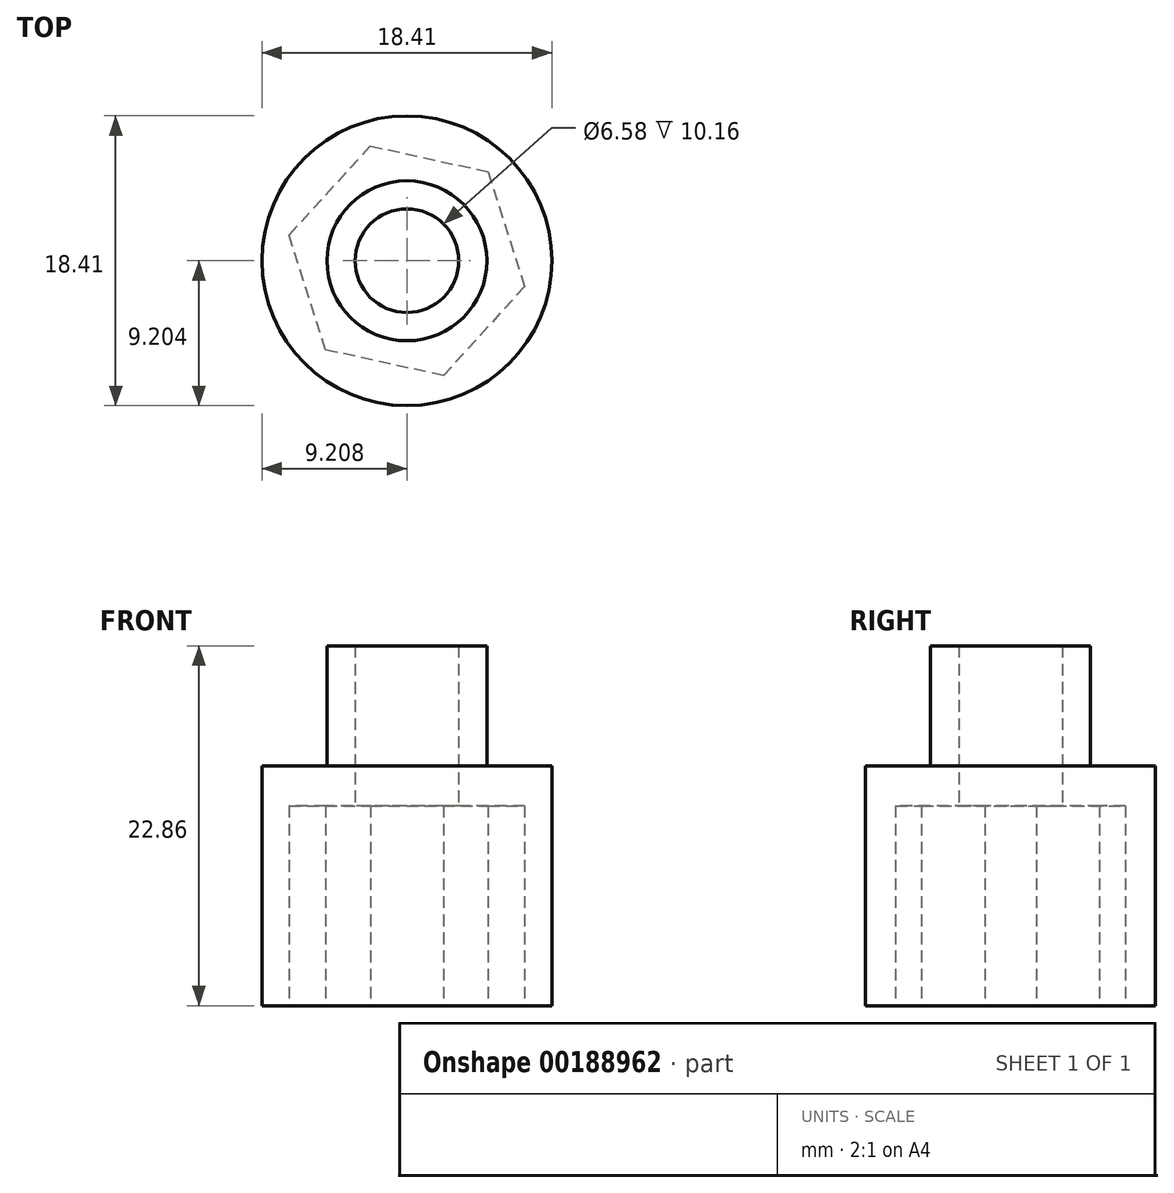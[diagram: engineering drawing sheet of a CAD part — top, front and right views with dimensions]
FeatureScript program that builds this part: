
annotation { "Feature Type Name" : "Feature", "Feature Type Description" : "" }
export const myFeature = defineFeature(function(context is Context, id is Id, definition is map)
    precondition{}
    {
        {
            var Q0;
            Q0=qCreatedBy(makeId("Top.planeOp"),FACE);
            var sketch = newSketch(context, id + "F0", { "sketchPlane" : qUnion([Q0])});
            skCircle(sketch, "E0.cCircle", {"center": v(-50.73, -47.86) * mm, "radius": 6.63 * mm, "construction": true});
            skLineSegment(sketch, "E0.0", {"start": v(-43.25, -49.5) * mm, "end": v(-48.4, -55.15) * mm});
            skLineSegment(sketch, "E0.1", {"start": v(-48.4, -55.15) * mm, "end": v(-55.89, -53.51) * mm});
            skLineSegment(sketch, "E0.2", {"start": v(-55.89, -53.51) * mm, "end": v(-58.21, -46.22) * mm});
            skLineSegment(sketch, "E0.3", {"start": v(-58.21, -46.22) * mm, "end": v(-53.05, -40.56) * mm});
            skLineSegment(sketch, "E0.4", {"start": v(-53.05, -40.56) * mm, "end": v(-45.57, -42.2) * mm});
            skLineSegment(sketch, "E0.5", {"start": v(-45.57, -42.2) * mm, "end": v(-43.25, -49.5) * mm});
            skPoint(sketch, "E0.0.midPoint", {"position": v(-45.83, -52.32) * mm});
            skCircle(sketch, "E1", {"center": v(-50.73, -47.86) * mm, "radius": 9.2 * mm});
            skSolve(sketch);
        }
        {
            var Q0;
            Q0=qSketchRegion(id+"F0",true);
            extrude(context, id + "F1", {"entities" : qUnion([Q0]), "depth" : 12.7 * mm});
        }
        {
            var Q0;
            Q0=makeQuery(id+"F1.opExtrude","CAP_FACE",FACE,{"disambiguationData":[OSD([sQuery(id+"F0.wireOp",EDGE,"E0.0"),sQuery(id+"F0.wireOp",EDGE,"E0.1"),sQuery(id+"F0.wireOp",EDGE,"E0.2"),sQuery(id+"F0.wireOp",EDGE,"E0.3"),sQuery(id+"F0.wireOp",EDGE,"E0.4"),sQuery(id+"F0.wireOp",EDGE,"E0.5"),sQuery(id+"F0.wireOp",EDGE,"E1")])],"isStart":false});
            var sketch = newSketch(context, id + "F2", { "sketchPlane" : qUnion([Q0])});
            skCircle(sketch, "E2.0", {"center": v(-50.73, -47.86) * mm, "radius": 9.2 * mm});
            skCircle(sketch, "E3", {"center": v(-50.73, -47.86) * mm, "radius": 3.29 * mm});
            skCircle(sketch, "E4", {"center": v(-50.73, -47.86) * mm, "radius": 5.08 * mm});
            skSolve(sketch);
        }
        {
            var Q0;
            Q0=makeQuery(id+"F2.imprint","IMPRINT",FACE,{"disambiguationData":[TD([[makeQuery(id+"F2.imprint","IMPRINT",EDGE,{"derivedFrom":sQuery(id+"F2.wireOp",EDGE,"E2.0")}),1.0]])]});
            var Q1;
            Q1=makeQuery(id+"F2.imprint","IMPRINT",FACE,{"disambiguationData":[TD([[makeQuery(id+"F2.imprint","IMPRINT",EDGE,{"derivedFrom":sQuery(id+"F2.wireOp",EDGE,"E4")}),-1.0]])]});
            extrude(context, id + "F3", {"entities" : qUnion([Q0, Q1]), "operationType" : NewBodyOperationType.ADD, "depth" : 2.54 * mm});
        }
        {
            var Q0;
            Q0=makeQuery(id+"F2.imprint","IMPRINT",FACE,{"disambiguationData":[TD([[makeQuery(id+"F2.imprint","IMPRINT",EDGE,{"derivedFrom":sQuery(id+"F2.wireOp",EDGE,"E3")}),-1.0]])]});
            extrude(context, id + "F4", {"entities" : qUnion([Q0]), "operationType" : NewBodyOperationType.ADD, "depth" : 10.16 * mm});
        }
    });
